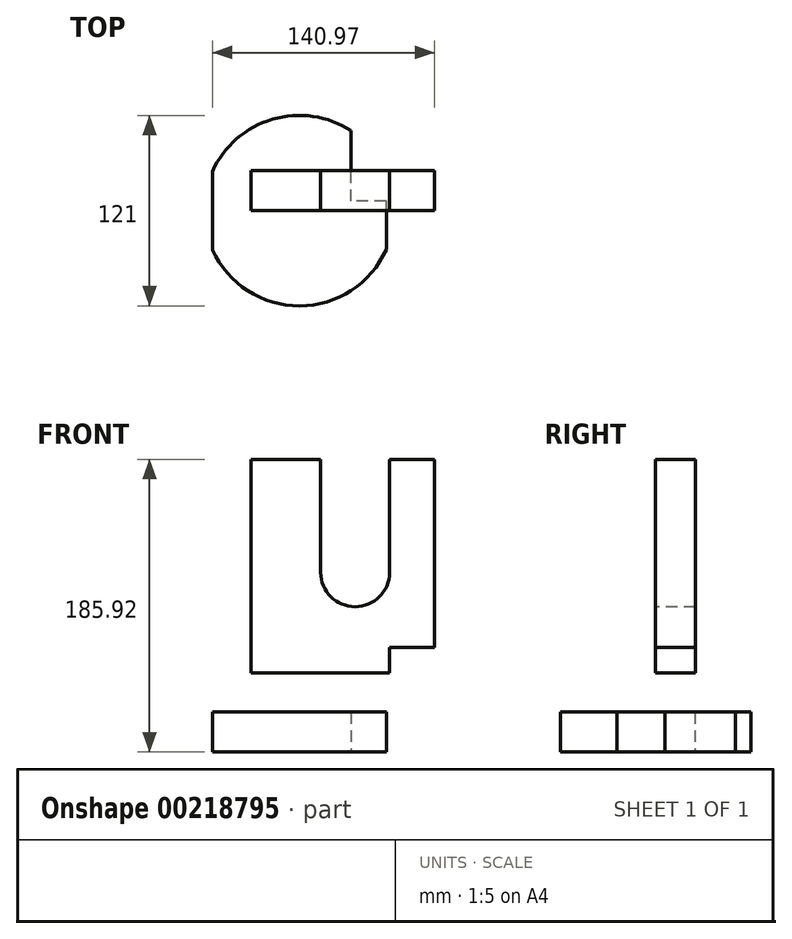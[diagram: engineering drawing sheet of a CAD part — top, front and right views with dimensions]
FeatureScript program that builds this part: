
annotation { "Feature Type Name" : "Feature", "Feature Type Description" : "" }
export const myFeature = defineFeature(function(context is Context, id is Id, definition is map)
    precondition{}
    {
        {
            var Q0;
            Q0=qCreatedBy(makeId("Top.planeOp"),FACE);
            var sketch = newSketch(context, id + "F0", { "sketchPlane" : qUnion([Q0])});
            skArc(sketch, "E0", {"start": v(32.87, 50.8) * mm, "mid": v(-17.07, 58.04) * mm, "end": v(-55.14, 24.91) * mm});
            skLineSegment(sketch, "E1", {"start": v(55.25, -24.65) * mm, "end": v(55.25, 5.95) * mm});
            skLineSegment(sketch, "E2", {"start": v(55.25, 5.95) * mm, "end": v(32.87, 5.95) * mm});
            skLineSegment(sketch, "E3", {"start": v(32.87, 5.95) * mm, "end": v(32.87, 50.8) * mm});
            skLineSegment(sketch, "E4", {"start": v(-55.14, -24.91) * mm, "end": v(-55.14, 24.91) * mm});
            skArc(sketch, "E5.trimOffspring", {"start": v(-55.14, -24.91) * mm, "mid": v(0.14, -60.5) * mm, "end": v(55.25, -24.65) * mm});
            skSolve(sketch);
        }
        {
            var Q0;
            Q0 = qSketchRegion(id + "F0", true);
            extrude(context, id + "F1", {"entities" : qUnion([Q0]), "depth" : 25.4 * mm});
        }
        {
            var Q0;
            Q0=qCreatedBy(makeId("Front.planeOp"),FACE);
            var sketch = newSketch(context, id + "F2", { "sketchPlane" : qUnion([Q0])});
            skLineSegment(sketch, "E6", {"start": v(-30.57, 50.36) * mm, "end": v(57.26, 50.36) * mm});
            skLineSegment(sketch, "E7", {"start": v(57.26, 50.36) * mm, "end": v(57.26, 66.5) * mm});
            skLineSegment(sketch, "E8", {"start": v(57.26, 66.5) * mm, "end": v(85.83, 66.5) * mm});
            skLineSegment(sketch, "E9", {"start": v(85.83, 66.5) * mm, "end": v(85.83, 185.92) * mm});
            skLineSegment(sketch, "E10", {"start": v(85.83, 185.92) * mm, "end": v(57.26, 185.92) * mm});
            skLineSegment(sketch, "E11", {"start": v(57.26, 185.92) * mm, "end": v(57.26, 114.2) * mm});
            skLineSegment(sketch, "E12", {"start": v(13.55, 114.2) * mm, "end": v(13.55, 185.92) * mm});
            skLineSegment(sketch, "E13", {"start": v(13.55, 185.92) * mm, "end": v(-30.57, 185.92) * mm});
            skLineSegment(sketch, "E14", {"start": v(-30.57, 185.92) * mm, "end": v(-30.57, 50.36) * mm});
            skArc(sketch, "E15", {"start": v(13.55, 114.2) * mm, "mid": v(35.4, 92.35) * mm, "end": v(57.26, 114.2) * mm});
            skSolve(sketch);
        }
        {
            var Q0;
            Q0=makeQuery(id+"F2.imprint","IMPRINT",FACE,{"disambiguationData":[TD([[makeQuery(id+"F2.imprint","IMPRINT",EDGE,{"derivedFrom":sQuery(id+"F2.wireOp",EDGE,"E6")}),1.0]])]});
            extrude(context, id + "F3", {"entities" : qUnion([Q0]), "oppositeDirection" : true, "depth" : 25.4 * mm});
        }
    });
